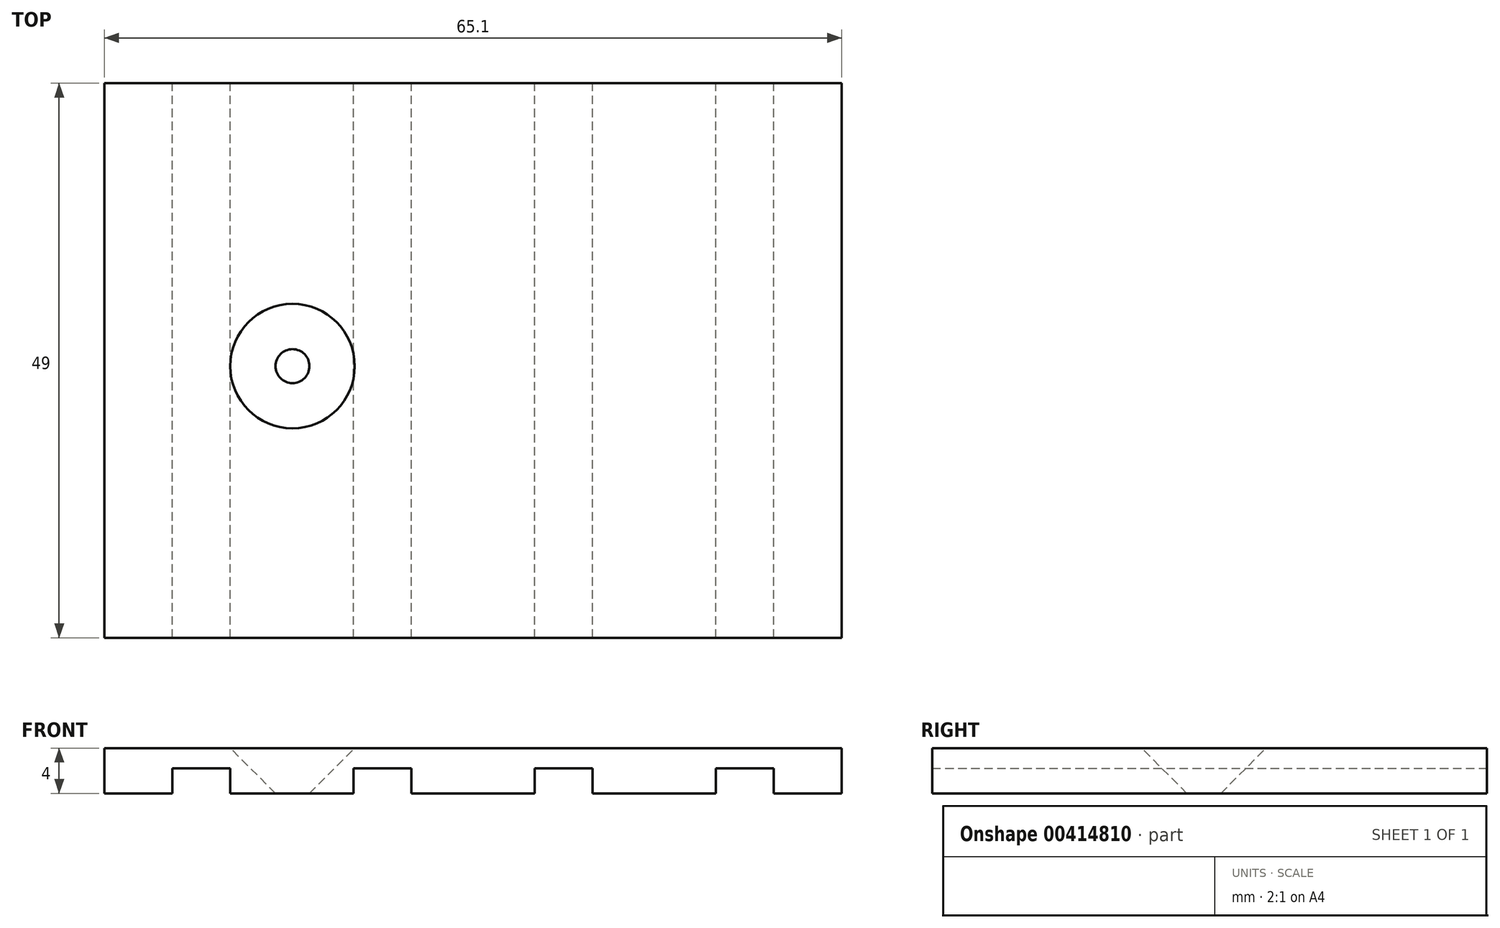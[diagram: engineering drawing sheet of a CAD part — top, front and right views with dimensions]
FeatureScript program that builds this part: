
annotation { "Feature Type Name" : "Feature", "Feature Type Description" : "" }
export const myFeature = defineFeature(function(context is Context, id is Id, definition is map)
    precondition{}
    {
        {
            var Q0;
            Q0=qCreatedBy(makeId("Front.planeOp"),FACE);
            var sketch = newSketch(context, id + "F0", { "sketchPlane" : qUnion([Q0])});
            skLineSegment(sketch, "E0.bottom", {"start": v(-32.55, 4) * mm, "end": v(0, 4) * mm});
            skLineSegment(sketch, "E0.top", {"start": v(-32.55, 0) * mm, "end": v(0, 0) * mm});
            skLineSegment(sketch, "E0.left", {"start": v(-32.55, 4) * mm, "end": v(-32.55, 0) * mm});
            skLineSegment(sketch, "E0.right", {"start": v(0, 4) * mm, "end": v(0, 0) * mm});
            skLineSegment(sketch, "E1.bottom", {"start": v(-5.45, 0) * mm, "end": v(-10.55, 0) * mm});
            skLineSegment(sketch, "E1.top", {"start": v(-5.45, 2.2) * mm, "end": v(-10.55, 2.2) * mm});
            skLineSegment(sketch, "E1.left", {"start": v(-5.45, 0) * mm, "end": v(-5.45, 2.2) * mm});
            skLineSegment(sketch, "E1.right", {"start": v(-10.55, 0) * mm, "end": v(-10.55, 2.2) * mm});
            skLineSegment(sketch, "E2.bottom", {"start": v(-26.55, 0) * mm, "end": v(-21.45, 0) * mm});
            skLineSegment(sketch, "E2.top", {"start": v(-26.55, 2.2) * mm, "end": v(-21.45, 2.2) * mm});
            skLineSegment(sketch, "E2.left", {"start": v(-26.55, 0) * mm, "end": v(-26.55, 2.2) * mm});
            skLineSegment(sketch, "E2.right", {"start": v(-21.45, 0) * mm, "end": v(-21.45, 2.2) * mm});
            skLineSegment(sketch, "E3.MirrorCS", {"start": v(10.55, 0) * mm, "end": v(10.55, 2.2) * mm});
            skLineSegment(sketch, "E4.MirrorCS", {"start": v(5.45, 0) * mm, "end": v(5.45, 2.2) * mm});
            skLineSegment(sketch, "E5.MirrorCS", {"start": v(26.55, 0) * mm, "end": v(26.55, 2.2) * mm});
            skLineSegment(sketch, "E6.MirrorCS", {"start": v(21.45, 0) * mm, "end": v(21.45, 2.2) * mm});
            skLineSegment(sketch, "E7.MirrorCS", {"start": v(26.55, 2.2) * mm, "end": v(21.45, 2.2) * mm});
            skLineSegment(sketch, "E8.MirrorCS", {"start": v(32.55, 4) * mm, "end": v(32.55, 0) * mm});
            skLineSegment(sketch, "E9.MirrorCS", {"start": v(26.55, 0) * mm, "end": v(21.45, 0) * mm});
            skLineSegment(sketch, "E10.MirrorCS", {"start": v(5.45, 2.2) * mm, "end": v(10.55, 2.2) * mm});
            skLineSegment(sketch, "E11.MirrorCS", {"start": v(5.45, 0) * mm, "end": v(10.55, 0) * mm});
            skLineSegment(sketch, "E12.MirrorCS", {"start": v(32.55, 0) * mm, "end": v(0, 0) * mm});
            skLineSegment(sketch, "E13.MirrorCS", {"start": v(32.55, 4) * mm, "end": v(0, 4) * mm});
            skLineSegment(sketch, "E14", {"start": v(-16.28, 4) * mm, "end": v(-16.28, 0) * mm});
            skLineSegment(sketch, "E15", {"start": v(16.28, 4) * mm, "end": v(16.28, 0) * mm});
            skSolve(sketch);
        }
        {
            var Q0;
            {var subQ0=sQuery(id+"F0.wireOp",EDGE,"E0.left");Q0=makeQuery(id+"F0.imprint","IMPRINT",FACE,{"disambiguationData":[TD([[makeQuery(id+"F0.imprint","IMPRINT",EDGE,{"derivedFrom":subQ0}),1.0]])]});}
            var Q1;
            {var subQ0=sQuery(id+"F0.wireOp",EDGE,"E0.right");Q1=makeQuery(id+"F0.imprint","IMPRINT",FACE,{"disambiguationData":[TD([[makeQuery(id+"F0.imprint","IMPRINT",EDGE,{"derivedFrom":subQ0}),-1.0]])]});}
            var Q2;
            {var subQ3=sQuery(id+"F0.wireOp",EDGE,"E0.right");Q2=makeQuery(id+"F0.imprint","IMPRINT",FACE,{"disambiguationData":[TD([[makeQuery(id+"F0.imprint","IMPRINT",EDGE,{"derivedFrom":subQ3}),1.0]])]});}
            var Q3;
            {var subQ3=sQuery(id+"F0.wireOp",EDGE,"E5.MirrorCS");Q3=makeQuery(id+"F0.imprint","IMPRINT",FACE,{"disambiguationData":[TD([[makeQuery(id+"F0.imprint","IMPRINT",EDGE,{"derivedFrom":subQ3}),-1.0]])]});}
            extrude(context, id + "F1", {"entities" : qUnion([Q0, Q1, Q2, Q3]), "depth" : 49 * mm});
        }
        {
            var Q0;
            Q0=qCreatedBy(makeId("Top.planeOp"),FACE);
            var sketch = newSketch(context, id + "F2", { "sketchPlane" : qUnion([Q0])});
            skLineSegment(sketch, "E16.MirrorCS", {"start": v(-28.2, 63.6) * mm, "end": v(28, 63.6) * mm, "construction": true});
            skLineSegment(sketch, "E17.MirrorCS", {"start": v(-14.23, 0) * mm, "end": v(-14.23, 77.06) * mm, "construction": true});
            skLineSegment(sketch, "E18.MirrorCS", {"start": v(13.88, 0) * mm, "end": v(13.88, 76.78) * mm, "construction": true});
            skCircle(sketch, "E19", {"center": v(-15.95, -25) * mm, "radius": 1.5 * mm});
            skCircle(sketch, "E20.MirrorC", {"center": v(15.95, -25) * mm, "radius": 1.5 * mm});
            skSolve(sketch);
        }
        {
            var Q0;
            Q0=makeQuery(id+"F2.imprint","IMPRINT",FACE,{"disambiguationData":[TD([[makeQuery(id+"F2.imprint","IMPRINT",EDGE,{"derivedFrom":sQuery(id+"F2.wireOp",EDGE,"E19")}),1.0]])]});
            var Q1;
            Q1=makeQuery(id+"F2.imprint","IMPRINT",FACE,{"disambiguationData":[TD([[makeQuery(id+"F2.imprint","IMPRINT",EDGE,{"derivedFrom":sQuery(id+"F2.wireOp",EDGE,"u66GRWq7-H4sf-GD8N-AXet-6ul3mTwaJhn2")}),1.0]])]});
            extrude(context, id + "F3", {"entities" : qUnion([Q0, Q1]), "operationType" : NewBodyOperationType.REMOVE, "oppositeDirection" : true, "depth" : 25 * mm, "hasSecondDirection" : true, "secondDirectionOppositeDirection" : false, "secondDirectionDepth" : 25 * mm});
        }
        {
            var Q0;
            Q0=makeQuery(id+"F2.imprint","IMPRINT",FACE,{"disambiguationData":[TD([[makeQuery(id+"F2.imprint","IMPRINT",EDGE,{"derivedFrom":sQuery(id+"F2.wireOp",EDGE,"E19")}),1.0]])]});
            var Q1;
            Q1=makeQuery(id+"F2.imprint","IMPRINT",FACE,{"disambiguationData":[TD([[makeQuery(id+"F2.imprint","IMPRINT",EDGE,{"derivedFrom":sQuery(id+"F2.wireOp",EDGE,"E20.MirrorC")}),-1.0]])]});
            extrude(context, id + "F4", {"entities" : qUnion([Q0, Q1]), "operationType" : NewBodyOperationType.REMOVE, "depth" : 12.4 * mm});
        }
        {
            var Q0;
            Q0=makeQuery(id+"F4.boolean.opBoolean","INTERSECT",EDGE,{"derivedFrom":[makeQuery(id+"F1.opExtrude","SWEPT_FACE",FACE,{"disambiguationData":[OSD([sQuery(id+"F0.wireOp",EDGE,"E0.bottom"),sQuery(id+"F0.wireOp",EDGE,"E13.MirrorCS")])]}),makeQuery(id+"F4.opExtrude","SWEPT_FACE",FACE,{"disambiguationData":[OSD([sQuery(id+"F2.wireOp",EDGE,"E20.MirrorC")])]})]});
            var Q1;
            Q1=makeQuery(id+"F3.boolean.opBoolean","INTERSECT",EDGE,{"derivedFrom":[makeQuery(id+"F1.opExtrude","SWEPT_FACE",FACE,{"disambiguationData":[OSD([sQuery(id+"F0.wireOp",EDGE,"E0.bottom"),sQuery(id+"F0.wireOp",EDGE,"E13.MirrorCS")])]}),makeQuery(id+"F3.opExtrude","SWEPT_FACE",FACE,{"disambiguationData":[OSD([sQuery(id+"F2.wireOp",EDGE,"E19")])]})]});
            chamfer(context, id + "F5", {"entities" : qUnion([Q0, Q1]), "width" : 4 * mm, "tangentPropagation" : true});
        }
    });
